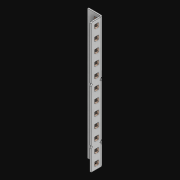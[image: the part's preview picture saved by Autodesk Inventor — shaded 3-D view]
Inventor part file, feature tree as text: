
AUTODESK INVENTOR PART (.ipt)
format: ipt  version: 2021 (Build 250183000, 183)  size: 1,134,592 bytes
history: native  units: in
note: dims shown in document units (in); Inventor stores cm internally (conversion verified against a paired STEP export)
features: extrude x26, other x24, sketch x4, pattern_linear x2, sheet_metal_op x1
ambient origin geometry x8: Origin, YZ Plane, XZ Plane, XY Plane, X Axis, Y Axis, Z Axis, Center Point
bodies: Solid1 (feature_tree)
feature tree (57):
  pattern_linear  "Rectangular Pattern1"  Spacing1=0.5in  [1 undecoded]
  pattern_linear  "Rectangular Pattern3"  Count1=12  [1 undecoded]
  extrude  "Extrusion1"  Depth=0.5in
  extrude  "Extrusion2"  Depth=0.5in
  sketch  "Sketch1"  dims[d0=0.182in]
  other  "Srf1"
  sketch  "Sketch3"  dims[d1=0.063in d2=0.0in]
  other  "Srf3"
  other  "Srf4"
  other  "Srf5"
  other  "Srf6"
  other  "Srf7"
  other  "Srf8"
  other  "Srf9"
  other  "Srf10"
  other  "Srf11"
  other  "Srf12"
  other  "Srf13"
  other  "Srf14"
  other  "Srf142"
  other  "Srf143"
  other  "Srf144"
  other  "Srf145"
  other  "Srf146"
  other  "Srf147"
  other  "Srf148"
  other  "Srf149"
  other  "Srf150"
  other  "Srf151"
  other  "Srf152"
  sketch  "Sketch4"  dims[d6=0.182in]
  sketch  "Sketch5"  dims[d7=0.063in d8=0.0in d11=0.5in d12=0.3937in d14=0.5in d18=4.7244in d20=0.5in d21=11.5in d22=0.0in d23=0.841in d24=0.0in]
  sheet_metal_op  "Fold1"
  extrude  "ExtrusionSrf1"  TaperAngle=0.0deg  [1 undecoded]
  extrude  "ExtrusionSrf3"  Depth=0.5in TaperAngle=0.0deg
  extrude  "ExtrusionSrf4"  [1 undecoded]
  extrude  "ExtrusionSrf5"  [1 undecoded]
  extrude  "ExtrusionSrf6"  [1 undecoded]
  extrude  "ExtrusionSrf7"  [1 undecoded]
  extrude  "ExtrusionSrf8"  [1 undecoded]
  extrude  "ExtrusionSrf9"  [1 undecoded]
  extrude  "ExtrusionSrf10"  [1 undecoded]
  extrude  "ExtrusionSrf11"  [1 undecoded]
  extrude  "ExtrusionSrf12"  [1 undecoded]
  extrude  "ExtrusionSrf13"  [1 undecoded]
  extrude  "ExtrusionSrf14"  [1 undecoded]
  extrude  "ExtrusionSrf142"  [1 undecoded]
  extrude  "ExtrusionSrf143"  [1 undecoded]
  extrude  "ExtrusionSrf144"  [1 undecoded]
  extrude  "ExtrusionSrf145"  [1 undecoded]
  extrude  "ExtrusionSrf146"  [1 undecoded]
  extrude  "ExtrusionSrf147"  [1 undecoded]
  extrude  "ExtrusionSrf148"  [1 undecoded]
  extrude  "ExtrusionSrf149"  [1 undecoded]
  extrude  "ExtrusionSrf150"  [1 undecoded]
  extrude  "ExtrusionSrf151"  [1 undecoded]
  extrude  "ExtrusionSrf152"  [1 undecoded]
note: 25 required parameter values undecoded (feature->parameter linkage not recoverable at this tier; creation-order binding heuristic only, values carry confidence <= 0.55)
